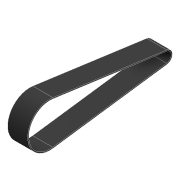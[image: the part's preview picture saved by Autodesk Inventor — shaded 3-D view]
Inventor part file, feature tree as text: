
AUTODESK INVENTOR PART (.ipt)
format: ipt  version: 2022 (Build 260153000, 153)  size: 97,792 bytes
history: native  units: mm
features: other x1, extrude x1, sketch x1
ambient origin geometry x8: Origin, YZ Plane, XZ Plane, XY Plane, X Axis, Y Axis, Z Axis, Center Point
bodies: Body1 (feature_tree)
feature tree (3):
  other  "Твердое тело1"
  extrude  "Выдавливание1"  Depth=21.0mm
  sketch  "Эскиз1"
